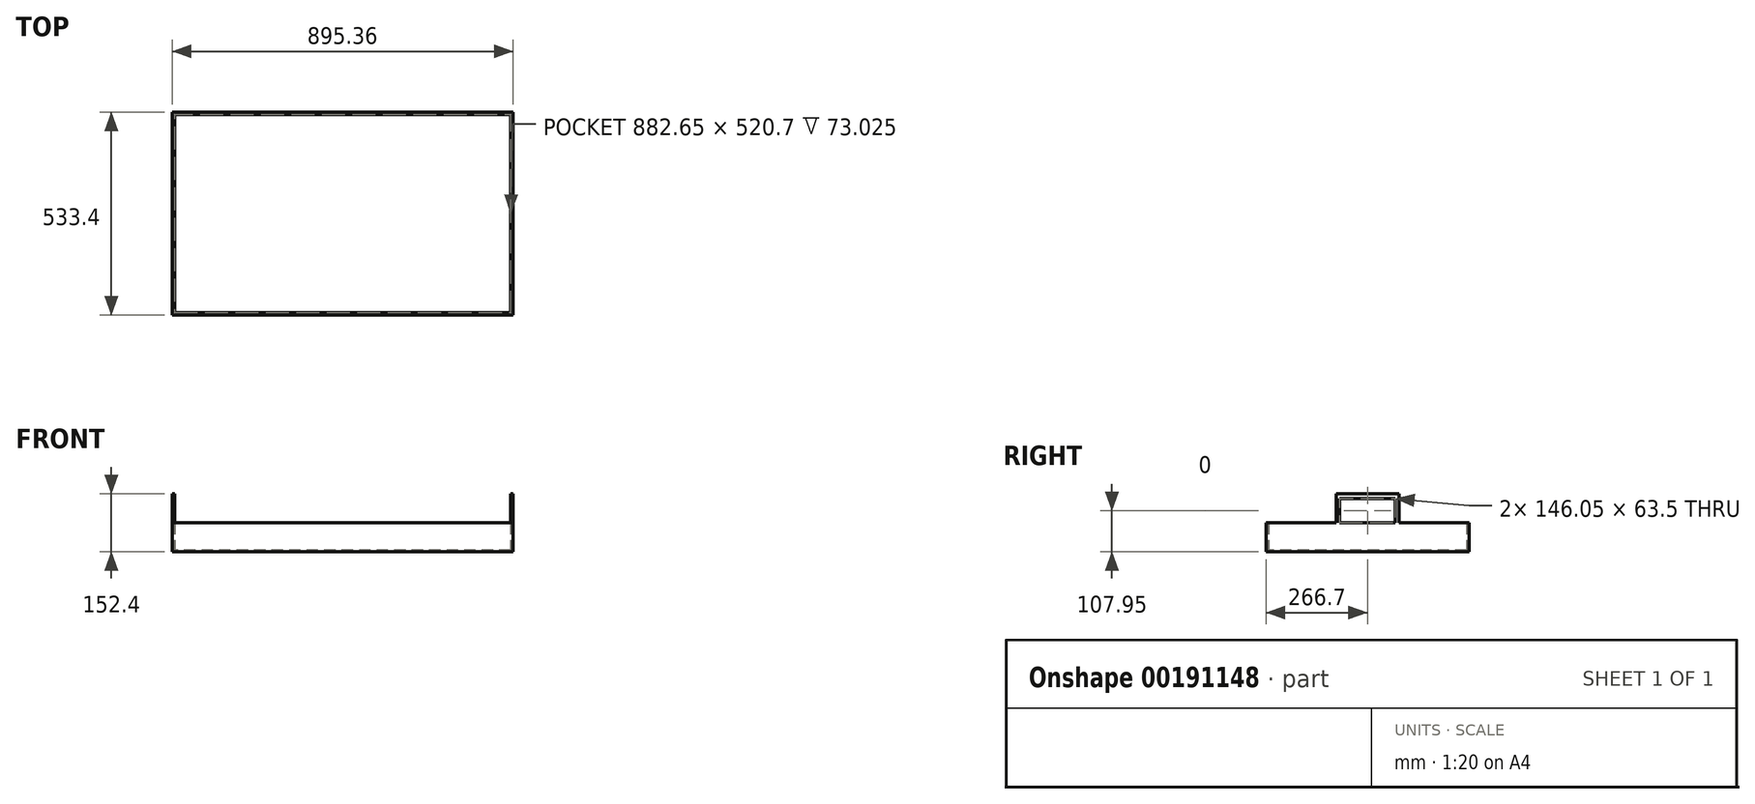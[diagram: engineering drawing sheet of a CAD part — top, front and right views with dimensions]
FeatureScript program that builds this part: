
annotation { "Feature Type Name" : "Feature", "Feature Type Description" : "" }
export const myFeature = defineFeature(function(context is Context, id is Id, definition is map)
    precondition{}
    {
        {
            var Q0;
            Q0=qCreatedBy(makeId("Top.planeOp"),FACE);
            var sketch = newSketch(context, id + "F0", { "sketchPlane" : qUnion([Q0])});
            skLineSegment(sketch, "E0.bottom", {"start": v(447.68, 266.7) * mm, "end": v(-447.68, 266.7) * mm});
            skLineSegment(sketch, "E0.top", {"start": v(447.68, -266.7) * mm, "end": v(-447.68, -266.7) * mm});
            skLineSegment(sketch, "E0.left", {"start": v(447.68, 266.7) * mm, "end": v(447.68, -266.7) * mm});
            skPoint(sketch, "E0.middle", {"position": v(0, 0) * mm});
            skLineSegment(sketch, "E1", {"start": v(-447.68, 266.7) * mm, "end": v(-447.68, -266.7) * mm});
            skLineSegment(sketch, "E2.bottom", {"start": v(441.32, 260.35) * mm, "end": v(-441.33, 260.35) * mm});
            skLineSegment(sketch, "E2.top", {"start": v(441.32, -260.35) * mm, "end": v(-441.33, -260.35) * mm});
            skLineSegment(sketch, "E2.left", {"start": v(441.32, 260.35) * mm, "end": v(441.32, -260.35) * mm});
            skLineSegment(sketch, "E2.right", {"start": v(-441.33, 260.35) * mm, "end": v(-441.33, -260.35) * mm});
            skSolve(sketch);
        }
        {
            var Q0;
            Q0=makeQuery(id+"F0.imprint","IMPRINT",FACE,{"disambiguationData":[TD([[makeQuery(id+"F0.imprint","IMPRINT",EDGE,{"derivedFrom":sQuery(id+"F0.wireOp",EDGE,"E0.bottom")}),1.0]])]});
            extrude(context, id + "F1", {"entities" : qUnion([Q0]), "depth" : 76.2 * mm});
        }
        {
            var Q0;
            Q0=makeQuery(id+"F0.imprint","IMPRINT",FACE,{"disambiguationData":[TD([[makeQuery(id+"F0.imprint","IMPRINT",EDGE,{"derivedFrom":sQuery(id+"F0.wireOp",EDGE,"E2.bottom")}),1.0]])]});
            extrude(context, id + "F2", {"entities" : qUnion([Q0]), "operationType" : NewBodyOperationType.ADD, "depth" : 3.17 * mm});
        }
        {
            var Q0;
            Q0=makeQuery(id+"F1.opExtrude","CAP_FACE",FACE,{"disambiguationData":[OSD([sQuery(id+"F0.wireOp",EDGE,"E0.bottom"),sQuery(id+"F0.wireOp",EDGE,"E0.top"),sQuery(id+"F0.wireOp",EDGE,"E0.left"),sQuery(id+"F0.wireOp",EDGE,"E1"),sQuery(id+"F0.wireOp",EDGE,"E2.bottom"),sQuery(id+"F0.wireOp",EDGE,"E2.top"),sQuery(id+"F0.wireOp",EDGE,"E2.left"),sQuery(id+"F0.wireOp",EDGE,"E2.right")])],"isStart":false});
            var sketch = newSketch(context, id + "F3", { "sketchPlane" : qUnion([Q0])});
            skLineSegment(sketch, "E3", {"start": v(0, 0) * mm, "end": v(-441.33, 0) * mm});
            skLineSegment(sketch, "E4", {"start": v(-441.33, 0) * mm, "end": v(-447.68, 0) * mm});
            skLineSegment(sketch, "E5.bottom", {"start": v(-441.33, 82.55) * mm, "end": v(-447.68, 82.55) * mm});
            skLineSegment(sketch, "E5.top", {"start": v(-441.33, -82.55) * mm, "end": v(-447.68, -82.55) * mm});
            skLineSegment(sketch, "E5.left", {"start": v(-441.33, 82.55) * mm, "end": v(-441.33, -82.55) * mm});
            skLineSegment(sketch, "E5.right", {"start": v(-447.68, 82.55) * mm, "end": v(-447.68, -82.55) * mm});
            skPoint(sketch, "E5.middle", {"position": v(-444.5, 0) * mm});
            skLineSegment(sketch, "E6.MirrorCS", {"start": v(441.33, 0) * mm, "end": v(447.68, 0) * mm});
            skLineSegment(sketch, "E7.MirrorCS", {"start": v(441.33, 82.55) * mm, "end": v(447.68, 82.55) * mm});
            skLineSegment(sketch, "E8.MirrorCS", {"start": v(441.33, -82.55) * mm, "end": v(447.68, -82.55) * mm});
            skLineSegment(sketch, "E9.MirrorCS", {"start": v(441.33, 82.55) * mm, "end": v(441.33, -82.55) * mm});
            skLineSegment(sketch, "E10.MirrorCS", {"start": v(447.68, 82.55) * mm, "end": v(447.68, -82.55) * mm});
            skPoint(sketch, "E11.MirrorP", {"position": v(444.5, 0) * mm});
            skSolve(sketch);
        }
        {
            var Q0;
            Q0 = qSketchRegion(id + "F3", true);
            extrude(context, id + "F4", {"entities" : qUnion([Q0]), "operationType" : NewBodyOperationType.ADD, "depth" : 76.2 * mm});
        }
        {
            var Q0;
            Q0=makeQuery(id+"F4.boolean.opBoolean","MERGE",FACE,{"derivedFrom":[makeQuery(id+"F1.opExtrude","SWEPT_FACE",FACE,{"disambiguationData":[OSD([sQuery(id+"F0.wireOp",EDGE,"E1")])]}),makeQuery(id+"F4.opExtrude","SWEPT_FACE",FACE,{"disambiguationData":[OSD([sQuery(id+"F3.wireOp",EDGE,"E5.right")])]})]});
            var sketch = newSketch(context, id + "F5", { "sketchPlane" : qUnion([Q0])});
            skLineSegment(sketch, "E12", {"start": v(-82.55, 76.2) * mm, "end": v(-73.03, 76.2) * mm});
            skLineSegment(sketch, "E13.bottom", {"start": v(-73.03, 76.2) * mm, "end": v(73.02, 76.2) * mm});
            skLineSegment(sketch, "E13.top", {"start": v(-73.03, 139.7) * mm, "end": v(73.02, 139.7) * mm});
            skLineSegment(sketch, "E13.left", {"start": v(-73.03, 76.2) * mm, "end": v(-73.03, 139.7) * mm});
            skLineSegment(sketch, "E13.right", {"start": v(73.02, 76.2) * mm, "end": v(73.02, 139.7) * mm});
            skSolve(sketch);
        }
        {
            var Q0;
            Q0 = qSketchRegion(id + "F5", true);
            extrude(context, id + "F6", {"entities" : qUnion([Q0]), "operationType" : NewBodyOperationType.REMOVE, "endBound" : BoundingType.THROUGH_ALL, "oppositeDirection" : true, "depth" : 25.4 * mm});
        }
    });
